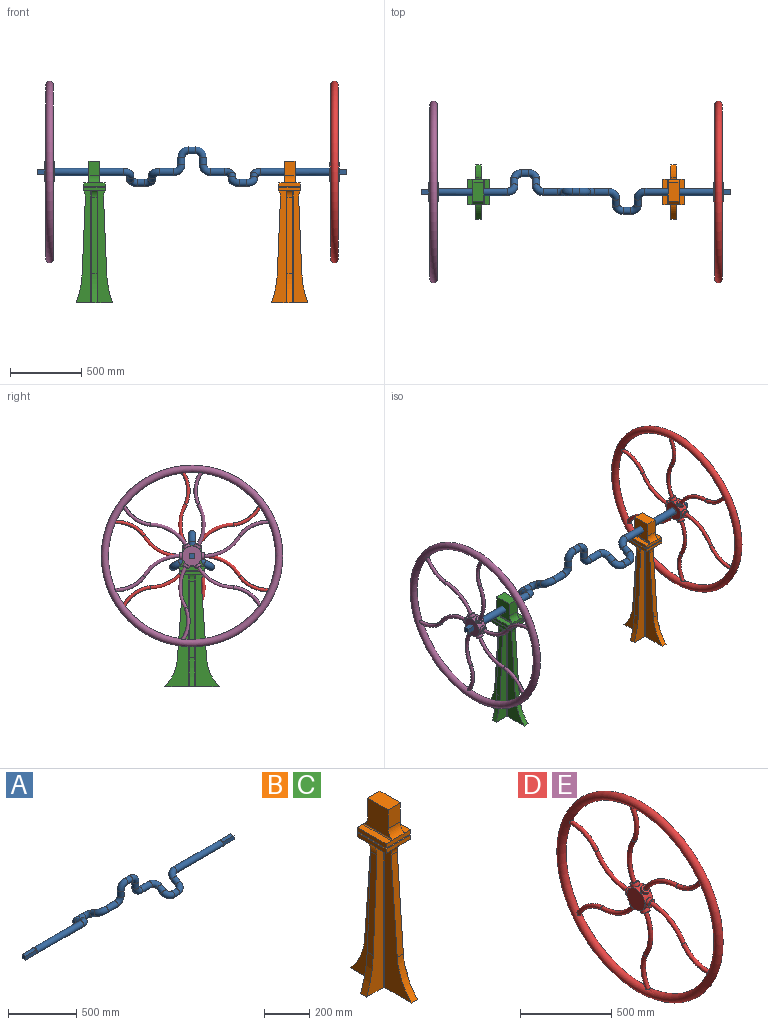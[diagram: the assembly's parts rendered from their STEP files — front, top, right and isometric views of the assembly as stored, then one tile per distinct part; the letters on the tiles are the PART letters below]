
ASSEMBLY  parts=5 mates=4
PART A: 43 faces, bbox 2165.4x320.9x287.7 mm
  f0: plane 35.92x7.44mm, normal (-1,0,0), area 184.1mm2, adj f32,f38
  f1: plane 35.92x7.44mm, normal (-1,0,0), area 184.1mm2, adj f32,f40
  f2: plane 35.92x7.44mm, normal (-1,0,0), area 184.1mm2, adj f32,f39
  f3: plane 35.92x7.44mm, normal (1,0,0), area 184.1mm2, adj f8,f33
  f4: plane 35.92x7.44mm, normal (1,0,0), area 184.1mm2, adj f8,f36
  f5: plane 35.92x7.44mm, normal (1,0,0), area 184.1mm2, adj f8,f35
  f6: plane 35.92x7.44mm, normal (1,0,0), area 184.1mm2, adj f8,f34
  f7: plane 35.92x7.44mm, normal (-1,0,0), area 184.1mm2, adj f32,f41
  f8: cylinder r=25.4mm len=482.6mm, axis (-1,0,0), area 77019.5mm2, adj f3,f4,f5,f6,f9
  f9: torus R=50.8mm, axis (0,-0.5,0.87), area 12734.9mm2, adj f8,f10
  f10: cylinder r=25.4mm len=69.39mm, axis (0,-0.87,-0.5), area 8107.3mm2, adj f9,f11
  f11: torus R=50.8mm, axis (0,0.5,-0.87), area 12734.9mm2, adj f10,f12
  f12: cylinder r=25.4mm len=50.8mm, axis (-1,0,0), area 8107.3mm2, adj f11,f13
  f13: torus R=50.8mm, axis (0,0.5,-0.87), area 12734.9mm2, adj f12,f14
  f14: cylinder r=25.4mm len=69.39mm, axis (0,0.87,0.5), area 8107.3mm2, adj f13,f15
  f15: torus R=50.8mm, axis (0,-0.5,0.87), area 12734.9mm2, adj f14,f16
  f16: cylinder r=25.4mm len=101.6mm, axis (-1,0,0), area 16214.6mm2, adj f15,f17
  f17: torus R=50.8mm, axis (0,1,0), area 12734.9mm2, adj f16,f18
  f18: cylinder r=25.4mm len=50.8mm, axis (0,0,1), area 8107.3mm2, adj f17,f19
  f19: torus R=50.8mm, axis (0,-1,0), area 12734.9mm2, adj f18,f20
  f20: cylinder r=25.4mm len=50.8mm, axis (-1,0,0), area 8107.3mm2, adj f19,f21
  f21: torus R=50.8mm, axis (0,-1,0), area 12734.9mm2, adj f20,f22
  f22: cylinder r=25.4mm len=50.8mm, axis (0,0,-1), area 8107.3mm2, adj f21,f23
  f23: torus R=50.8mm, axis (0,1,0), area 12734.9mm2, adj f22,f24
  f24: cylinder r=25.4mm len=101.6mm, axis (-1,0,0), area 16214.6mm2, adj f23,f25
  f25: torus R=50.8mm, axis (0,-0.5,-0.87), area 12734.9mm2, adj f24,f26
  f26: cylinder r=25.4mm len=69.39mm, axis (0,0.87,-0.5), area 8107.3mm2, adj f25,f27
  f27: torus R=50.8mm, axis (0,0.5,0.87), area 12734.9mm2, adj f26,f28
  f28: cylinder r=25.4mm len=50.8mm, axis (-1,0,0), area 8107.3mm2, adj f27,f29
  f29: torus R=50.8mm, axis (0,0.5,0.87), area 12734.9mm2, adj f28,f30
  f30: cylinder r=25.4mm len=69.39mm, axis (0,-0.87,0.5), area 8107.3mm2, adj f29,f31
  f31: torus R=50.8mm, axis (0,-0.5,-0.87), area 12734.9mm2, adj f30,f32
  f32: cylinder r=25.4mm len=482.6mm, axis (-1,0,0), area 77019.5mm2, adj f0,f1,f2,f7,f31
  f33: plane 117.48x35.92mm, normal (0,0,1), area 4219.8mm2, adj f3,f34,f36,f37
  f34: plane 117.48x35.92mm, normal (0,-1,0), area 4219.8mm2, adj f6,f33,f35,f37
  f35: plane 117.48x35.92mm, normal (0,0,-1), area 4219.8mm2, adj f5,f34,f36,f37
  f36: plane 117.48x35.92mm, normal (0,1,0), area 4219.8mm2, adj f4,f33,f35,f37
  f37: plane 35.92x35.92mm, normal (1,0,0), area 1290.3mm2, adj f33,f34,f35,f36
  f38: plane 117.48x35.92mm, normal (0,0,1), area 4219.8mm2, adj f0,f39,f41,f42
  f39: plane 117.48x35.92mm, normal (0,1,0), area 4219.8mm2, adj f2,f38,f40,f42
  f40: plane 117.48x35.92mm, normal (0,0,-1), area 4219.8mm2, adj f1,f39,f41,f42
  f41: plane 117.48x35.92mm, normal (0,-1,0), area 4219.8mm2, adj f7,f38,f40,f42
  f42: plane 35.92x35.92mm, normal (-1,0,0), area 1290.3mm2, adj f38,f39,f40,f41
PART B: 68 faces, bbox 254x381x990.6 mm
  f0: plane 177.8x33.02mm, normal (0,0,1), area 5871mm2, adj f34,f35,f37,f63
  f1: plane 782.32x166.37mm, normal (1,0,0), area 55129.6mm2, adj f3,f4,f5,f9,f44,f46
  f2: plane 782.32x166.37mm, normal (-1,0,0), area 55129.6mm2, adj f3,f4,f5,f9,f51,f54
  f3: cylinder r=331.51mm len=203.2mm, axis (-1,0,0), area 8616.5mm2, adj f1,f2,f4,f9
  f4: plane 533.4x38.1mm, normal (0,1,0.07), area 20374.3mm2, adj f1,f2,f3,f5
  f5: cylinder r=55.7mm len=50.8mm, axis (-1,0,0), area 2290.1mm2, adj f1,f2,f4,f26,f44,f51
  f6: cylinder r=55.7mm len=50.8mm, axis (-1,0,0), area 2290.1mm2, adj f7,f10,f11,f28,f42,f48
  f7: plane 533.4x38.1mm, normal (0,-1,0.07), area 20374.3mm2, adj f6,f8,f10,f11
  f8: cylinder r=331.51mm len=203.2mm, axis (-1,0,0), area 8616.5mm2, adj f7,f9,f10,f11
  f9: plane 381x254mm, normal (0,0,-1), area 22764mm2, adj f1,f2,f3,f8,f10,f11,f14,f15
  f10: plane 782.32x166.37mm, normal (1,0,0), area 55129.6mm2, adj f6,f7,f8,f9,f40,f42
  f11: plane 782.32x166.37mm, normal (-1,0,0), area 55129.6mm2, adj f6,f7,f8,f9,f48,f50
  f12: cylinder r=92.61mm len=50.8mm, axis (0,1,0), area 2035.4mm2, adj f13,f15,f16,f27,f47,f52
  f13: plane 533.4x38.1mm, normal (-1,0,0.04), area 20340.2mm2, adj f12,f14,f15,f16
  f14: cylinder r=655.8mm len=203.2mm, axis (0,1,0), area 7933.3mm2, adj f9,f13,f15,f16
  f15: plane 782.32x102.87mm, normal (0,-1,0), area 44428.4mm2, adj f9,f12,f13,f14,f47,f50
  f16: plane 782.32x102.87mm, normal (0,1,0), area 44428.4mm2, adj f9,f12,f13,f14,f52,f54
  f17: cylinder r=655.8mm len=203.2mm, axis (0,1,0), area 7933.3mm2, adj f9,f18,f20,f21
  f18: plane 533.4x38.1mm, normal (1,0,0.04), area 20340.2mm2, adj f17,f19,f20,f21
  f19: cylinder r=92.61mm len=50.8mm, axis (0,1,0), area 2035.4mm2, adj f18,f20,f21,f25,f39,f43
  f20: plane 782.32x102.87mm, normal (0,-1,0), area 44428.4mm2, adj f9,f17,f18,f19,f39,f40
  f21: plane 782.32x102.87mm, normal (0,1,0), area 44428.4mm2, adj f9,f17,f18,f19,f43,f46
  f22: plane 64.77x52.07mm, normal (0,0,-1), area 3372.6mm2, adj f26,f27,f51,f52
  f23: plane 64.77x52.07mm, normal (0,0,-1), area 3372.6mm2, adj f27,f28,f47,f48
  f24: plane 64.77x52.07mm, normal (0,0,-1), area 3372.6mm2, adj f25,f28,f39,f42
  f25: plane 177.8x22.23mm, normal (1,0,0), area 3951.6mm2, adj f19,f24,f26,f28,f29,f31
  f26: plane 152.4x22.23mm, normal (0,1,0), area 3387.1mm2, adj f5,f22,f25,f27,f29,f33
  f27: plane 177.8x22.23mm, normal (-1,0,0), area 3951.6mm2, adj f12,f22,f23,f26,f28,f32
  f28: plane 152.4x22.23mm, normal (0,-1,0), area 3387.1mm2, adj f6,f23,f24,f25,f27,f30
  f29: plane 64.77x52.07mm, normal (0,0,-1), area 3372.6mm2, adj f25,f26,f43,f44
  f30: plane 152.4x3.18mm, normal (0,-0.71,0.71), area 670mm2, adj f28,f31,f32,f64
  f31: plane 177.8x3.18mm, normal (0.71,0,0.71), area 784.1mm2, adj f25,f30,f33,f65
  f32: plane 177.8x3.18mm, normal (-0.71,0,0.71), area 784.1mm2, adj f27,f30,f33,f66
  f33: plane 152.4x3.18mm, normal (0,0.71,0.71), area 670mm2, adj f26,f31,f32,f67
  f34: plane 177.8x22.23mm, normal (1,0,0), area 3951.6mm2, adj f0,f35,f37,f65
  f35: plane 152.4x22.23mm, normal (0,1,0), area 3387.1mm2, adj f0,f34,f36,f38,f59,f67
  f36: plane 177.8x22.23mm, normal (-1,0,0), area 3951.6mm2, adj f35,f37,f38,f66
  f37: plane 152.4x22.23mm, normal (0,-1,0), area 3387.1mm2, adj f0,f34,f36,f38,f58,f64
  f38: plane 177.8x33.02mm, normal (0,0,1), area 5871mm2, adj f35,f36,f37,f62
  f39: cylinder r=5.08mm len=52.07mm, axis (1,0,0), area 407.2mm2, adj f19,f20,f24,f41
  f40: cylinder r=5.08mm len=782.32mm, axis (0,0,1), area 6242.6mm2, adj f9,f10,f20,f41
  f41: sphere r=5.08mm, area 40.5mm2, adj f39,f40,f42
  f42: cylinder r=5.08mm len=64.77mm, axis (0,-1,0), area 496.2mm2, adj f6,f10,f24,f41
  f43: cylinder r=5.08mm len=52.07mm, axis (-1,0,0), area 407.2mm2, adj f19,f21,f29,f45
  f44: cylinder r=5.08mm len=64.77mm, axis (0,-1,0), area 496.2mm2, adj f1,f5,f29,f45
  f45: sphere r=5.08mm, area 40.5mm2, adj f43,f44,f46
  f46: cylinder r=5.08mm len=782.32mm, axis (0,0,-1), area 6242.6mm2, adj f1,f9,f21,f45
  f47: cylinder r=5.08mm len=52.07mm, axis (1,0,0), area 407.2mm2, adj f12,f15,f23,f49
  f48: cylinder r=5.08mm len=64.77mm, axis (0,1,0), area 496.2mm2, adj f6,f11,f23,f49
  f49: sphere r=5.08mm, area 40.5mm2, adj f47,f48,f50
  f50: cylinder r=5.08mm len=782.32mm, axis (0,0,-1), area 6242.6mm2, adj f9,f11,f15,f49
  f51: cylinder r=5.08mm len=64.77mm, axis (0,1,0), area 496.2mm2, adj f2,f5,f22,f53
  f52: cylinder r=5.08mm len=52.07mm, axis (-1,0,0), area 407.2mm2, adj f12,f16,f22,f53
  f53: sphere r=5.08mm, area 40.5mm2, adj f51,f52,f54
  f54: cylinder r=5.08mm len=782.32mm, axis (0,0,1), area 6242.6mm2, adj f2,f9,f16,f53
  f55: plane 101.6x76.2mm, normal (0,1,0), area 7741.9mm2, adj f56,f59,f60,f61
  f56: plane 127x76.2mm, normal (0,0,1), area 9677.4mm2, adj f55,f57,f60,f61
  f57: plane 101.6x76.2mm, normal (0,-1,0), area 7741.9mm2, adj f56,f58,f60,f61
  f58: cylinder r=63.5mm len=86.36mm, axis (-1,0,0), area 4504.7mm2, adj f37,f57,f60,f61,f62,f63
  f59: cylinder r=63.5mm len=86.36mm, axis (-1,0,0), area 4504.7mm2, adj f35,f55,f60,f61,f62,f63
  f60: plane 165.87x147.32mm, normal (1,0,0), area 19260.2mm2, adj f55,f56,f57,f58,f59,f63
  f61: plane 165.87x147.32mm, normal (-1,0,0), area 19260.2mm2, adj f55,f56,f57,f58,f59,f62
  f62: cylinder r=5.08mm len=177.8mm, axis (0,-1,0), area 1382.5mm2, adj f38,f58,f59,f61
  f63: cylinder r=5.08mm len=177.8mm, axis (0,1,0), area 1382.5mm2, adj f0,f58,f59,f60
  f64: plane 152.4x3.18mm, normal (0,-0.71,-0.71), area 670mm2, adj f30,f37,f65,f66
  f65: plane 177.8x3.18mm, normal (0.71,0,-0.71), area 784.1mm2, adj f31,f34,f64,f67
  f66: plane 177.8x3.18mm, normal (-0.71,0,-0.71), area 784.1mm2, adj f32,f36,f64,f67
  f67: plane 152.4x3.18mm, normal (0,0.71,-0.71), area 670mm2, adj f33,f35,f65,f66
PART C: same geometry as B
PART D: 28 faces, bbox 63.5x1374.6x1374.6 mm
  f0: revolved ~214.85x114.04mm, area 18275mm2, adj f8,f27
  f1: revolved ~194.12x148.2mm, area 18275mm2, adj f12,f27
  f2: revolved ~235.15x62.56mm, area 18275mm2, adj f15,f27
  f3: revolved ~214.85x114.04mm, area 18275mm2, adj f18,f27
  f4: revolved ~194.12x148.2mm, area 18275mm2, adj f21,f27
  f5: revolved ~235.15x62.56mm, area 18275mm2, adj f24,f27
  f6: cylinder r=25.4mm len=50.8mm, axis (0,1,0), area 3417.5mm2, adj f7,f9
  f7: plane 50.8x50.8mm, normal (0,-1,0), area 1520.1mm2, adj f6,f8
  f8: torus R=285.23mm, axis (-1,0,0), area 23834.2mm2, adj f0,f7
  f9: cylinder r=69.85mm len=139.7mm, axis (1,0,0), area 15437.5mm2, adj f6,f10,f13,f16,f19,f22,f25,f26
  f10: cylinder r=25.4mm len=55.91mm, axis (0,0.5,-0.87), area 3417.5mm2, adj f9,f11
  f11: plane 50.8x43.99mm, normal (0,-0.5,0.87), area 1520.1mm2, adj f10,f12
  f12: torus R=285.23mm, axis (-1,0,0), area 23834.2mm2, adj f1,f11
  f13: cylinder r=25.4mm len=55.91mm, axis (0,-0.5,-0.87), area 3417.5mm2, adj f9,f14
  f14: plane 50.8x43.99mm, normal (0,0.5,0.87), area 1520.1mm2, adj f13,f15
  f15: torus R=285.23mm, axis (-1,0,0), area 23834.2mm2, adj f2,f14
  f16: cylinder r=25.4mm len=50.8mm, axis (0,-1,0), area 3417.5mm2, adj f9,f17
  f17: plane 50.8x50.8mm, normal (0,1,0), area 1520.1mm2, adj f16,f18
  f18: torus R=285.23mm, axis (-1,0,0), area 23834.2mm2, adj f3,f17
  f19: cylinder r=25.4mm len=55.91mm, axis (0,-0.5,0.87), area 3417.5mm2, adj f9,f20
  f20: plane 50.8x43.99mm, normal (0,0.5,-0.87), area 1520.1mm2, adj f19,f21
  f21: torus R=285.23mm, axis (-1,0,0), area 23834.2mm2, adj f4,f20
  f22: cylinder r=25.4mm len=55.91mm, axis (0,0.5,0.87), area 3417.5mm2, adj f9,f23
  f23: plane 50.8x43.99mm, normal (0,-0.5,-0.87), area 1520.1mm2, adj f22,f24
  f24: torus R=285.23mm, axis (-1,0,0), area 23834.2mm2, adj f5,f23
  f25: plane 139.7x139.7mm, normal (-1,0,0), area 15327.9mm2, adj f9
  f26: plane 139.7x139.7mm, normal (1,0,0), area 15327.9mm2, adj f9
  f27: torus R=609.6mm, axis (-1,0,0), area 607606.9mm2, adj f0,f1,f2,f3,f4,f5
PART E: same geometry as D
PLACE A t=(-161,70.33,793.86)mm
PLACE B t=(521.63,70.33,-121.29)mm
PLACE C t=(-843.62,70.33,-121.29)mm
PLACE D t=(835.95,70.33,793.86)mm
PLACE E rot(axis=(0,1,0),180deg) t=(-1157.95,70.33,793.86)mm
MATE fastened E.f9 <-> A.f32  axis (-1,0,0) through (-1189.7,70.33,793.86)mm
MATE fastened C.f60 <-> A.f32  axis (1,0,0) through (-805.52,70.33,793.86)mm
MATE fastened B.f61 <-> A.f8  axis (-1,0,0) through (483.53,70.33,793.86)mm
MATE fastened D.f9 <-> A.f8  axis (1,0,0) through (867.7,70.33,793.86)mm
